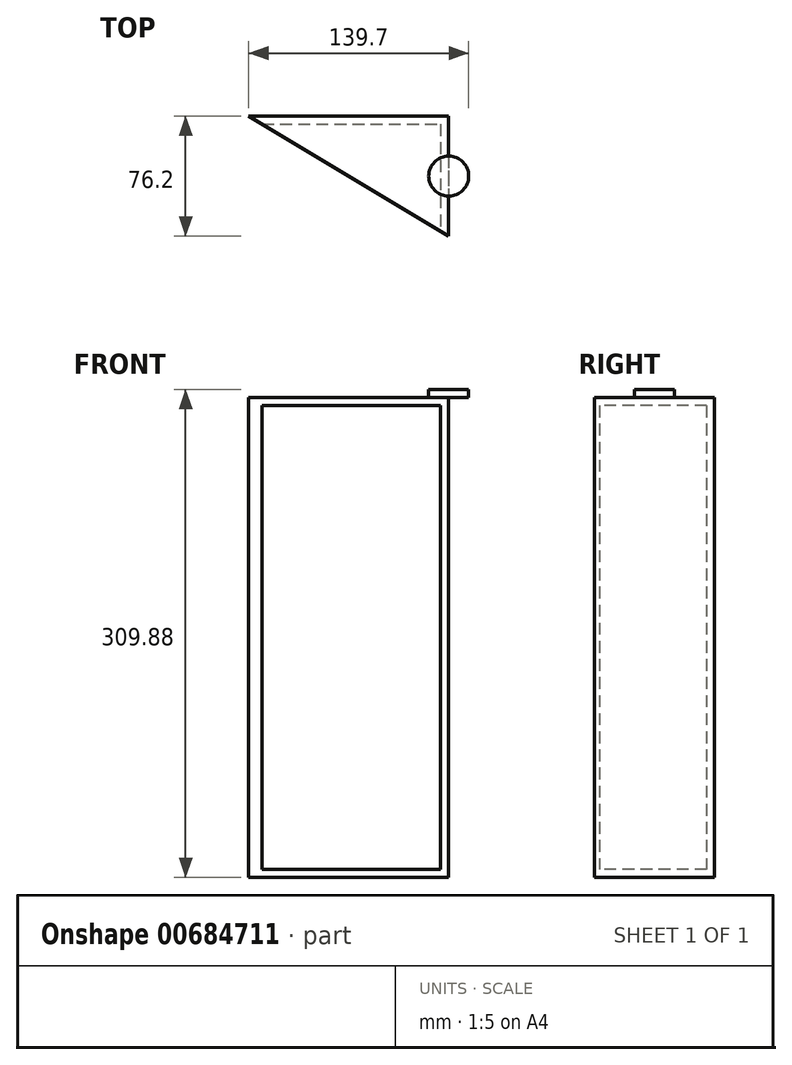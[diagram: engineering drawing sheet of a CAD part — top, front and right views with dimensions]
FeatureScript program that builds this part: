
annotation { "Feature Type Name" : "Feature", "Feature Type Description" : "" }
export const myFeature = defineFeature(function(context is Context, id is Id, definition is map)
    precondition{}
    {
        {
            var Q0;
            Q0=qCreatedBy(makeId("Top.planeOp"),FACE);
            var sketch = newSketch(context, id + "F0", { "sketchPlane" : qUnion([Q0])});
            skLineSegment(sketch, "E0", {"start": v(-87.69, 46.1) * mm, "end": v(39.31, 46.1) * mm});
            skArc(sketch, "E1", {"start": v(39.31, 46.1) * mm, "mid": v(77.41, 8) * mm, "end": v(39.31, -30.1) * mm});
            skLineSegment(sketch, "E2", {"start": v(39.31, 46.1) * mm, "end": v(39.31, -30.1) * mm});
            skLineSegment(sketch, "E3", {"start": v(-87.69, 46.1) * mm, "end": v(39.31, -30.1) * mm});
            skSolve(sketch);
        }
        {
            var Q0;
            Q0=makeQuery(id+"F0.imprint","IMPRINT",FACE,{"disambiguationData":[TD([[makeQuery(id+"F0.imprint","IMPRINT",EDGE,{"derivedFrom":sQuery(id+"F0.wireOp",EDGE,"E0")}),-1.0]])]});
            var Q1;
            Q1=makeQuery(id+"F0.imprint","IMPRINT",FACE,{"disambiguationData":[TD([[makeQuery(id+"F0.imprint","IMPRINT",EDGE,{"derivedFrom":sQuery(id+"F0.wireOp",EDGE,"E1")}),-1.0]])]});
            extrude(context, id + "F1", {"entities" : qUnion([Q0, Q1]), "depth" : 304.8 * mm, "offsetDistance" : 25.4 * mm});
        }
        {
            var Q0;
            Q0=makeQuery(id+"F1.opExtrude","SWEPT_FACE",FACE,{"disambiguationData":[OSD([sQuery(id+"F0.wireOp",EDGE,"E3")])]});
            shell(context, id + "F2", {"entities" : qUnion([Q0]), "thickness" : 5.08 * mm});
        }
        {
            var Q0;
            Q0=makeQuery(id+"F1.opExtrude","CAP_FACE",FACE,{"disambiguationData":[OSD([sQuery(id+"F0.wireOp",EDGE,"E0"),sQuery(id+"F0.wireOp",EDGE,"E1"),sQuery(id+"F0.wireOp",EDGE,"E3")])],"isStart":false});
            var sketch = newSketch(context, id + "F3", { "sketchPlane" : qUnion([Q0])});
            skCircle(sketch, "E4", {"center": v(39.31, 8) * mm, "radius": 12.7 * mm});
            skSolve(sketch);
        }
        {
            var Q0;
            Q0=makeQuery(id+"F3.imprint","IMPRINT",FACE,{"disambiguationData":[TD([[makeQuery(id+"F3.imprint","IMPRINT",EDGE,{"derivedFrom":sQuery(id+"F3.wireOp",EDGE,"E4")}),1.0]])]});
            extrude(context, id + "F4", {"entities" : qUnion([Q0]), "operationType" : NewBodyOperationType.ADD, "depth" : 5.08 * mm, "offsetDistance" : 25.4 * mm});
        }
    });
